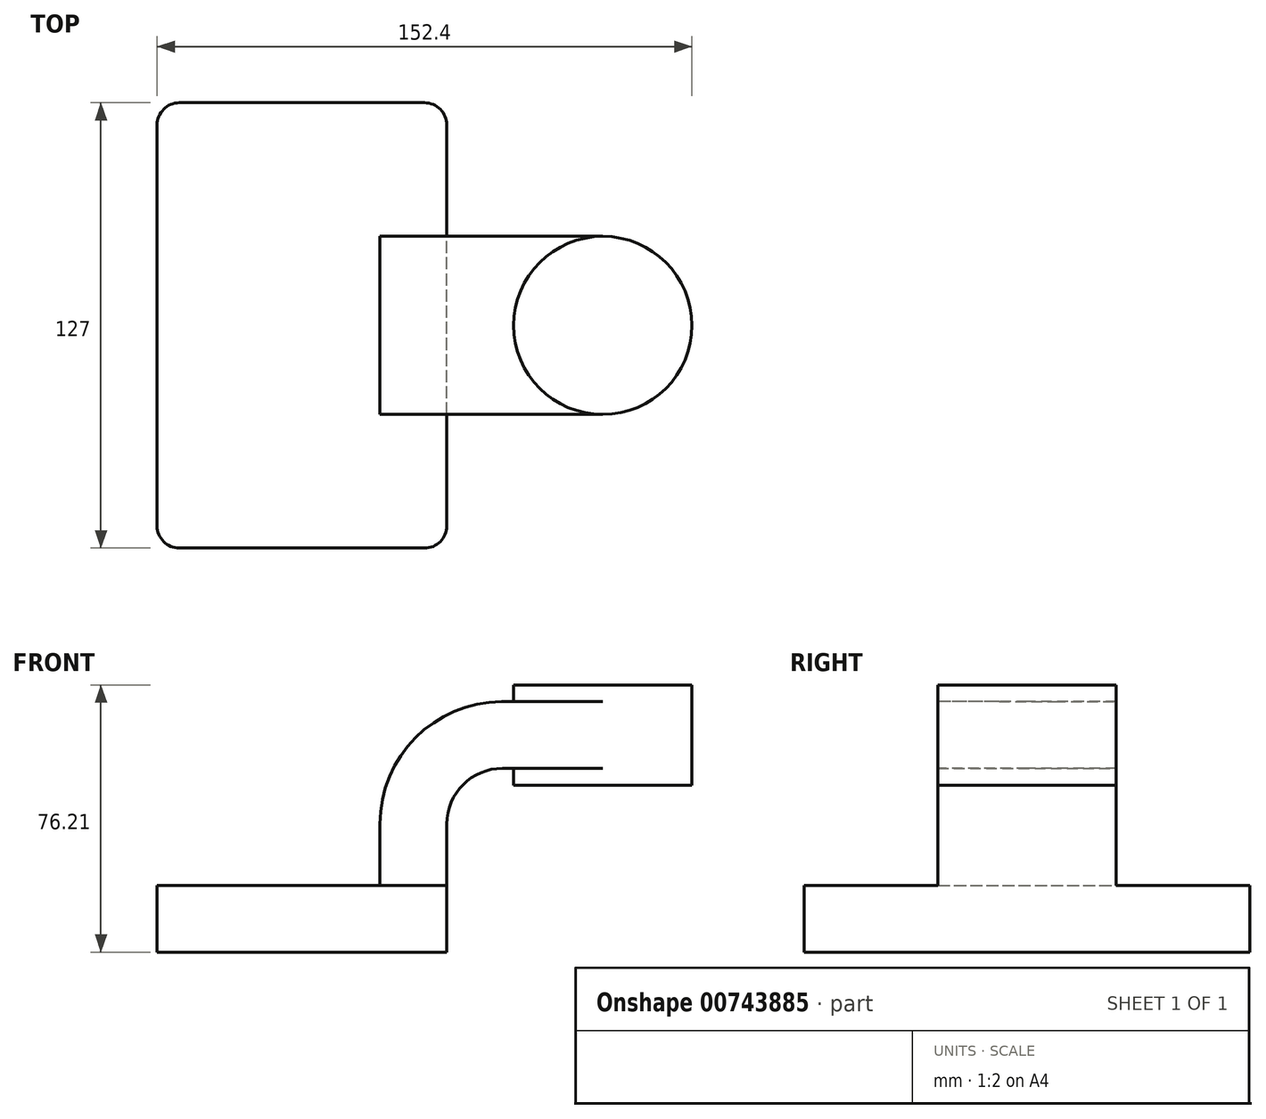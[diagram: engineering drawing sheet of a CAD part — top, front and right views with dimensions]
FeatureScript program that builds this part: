
annotation { "Feature Type Name" : "Feature", "Feature Type Description" : "" }
export const myFeature = defineFeature(function(context is Context, id is Id, definition is map)
    precondition{}
    {
        {
            var Q0;
            Q0=qCreatedBy(makeId("Front.planeOp"),FACE);
            var sketch = newSketch(context, id + "F0", { "sketchPlane" : qUnion([Q0])});
            skLineSegment(sketch, "E0.bottom", {"start": v(-41.28, -9.53) * mm, "end": v(41.28, -9.53) * mm});
            skLineSegment(sketch, "E0.top", {"start": v(-41.28, 9.53) * mm, "end": v(41.28, 9.53) * mm});
            skLineSegment(sketch, "E0.left", {"start": v(-41.28, -9.53) * mm, "end": v(-41.28, 9.53) * mm});
            skLineSegment(sketch, "E0.right", {"start": v(41.28, -9.53) * mm, "end": v(41.28, 9.53) * mm});
            skPoint(sketch, "E0.middle", {"position": v(0, 0) * mm});
            skLineSegment(sketch, "E1.bottom", {"start": v(60.33, 66.68) * mm, "end": v(111.12, 66.68) * mm});
            skLineSegment(sketch, "E1.top", {"start": v(60.33, 38.1) * mm, "end": v(111.12, 38.1) * mm});
            skLineSegment(sketch, "E1.left", {"start": v(60.33, 66.67) * mm, "end": v(60.33, 38.1) * mm});
            skLineSegment(sketch, "E1.right", {"start": v(111.12, 66.67) * mm, "end": v(111.12, 38.1) * mm});
            skPoint(sketch, "E1.middle", {"position": v(85.72, 52.39) * mm});
            skLineSegment(sketch, "E2", {"start": v(41.28, 9.53) * mm, "end": v(41.28, 27) * mm});
            skArc(sketch, "E3", {"start": v(41.28, 27) * mm, "mid": v(45.92, 38.23) * mm, "end": v(57.15, 42.88) * mm});
            skLineSegment(sketch, "E4", {"start": v(57.15, 42.88) * mm, "end": v(85.73, 42.88) * mm});
            skLineSegment(sketch, "E5.0", {"start": v(57.15, 61.93) * mm, "end": v(85.73, 61.93) * mm});
            skArc(sketch, "E5.1", {"start": v(22.23, 27) * mm, "mid": v(32.45, 51.7) * mm, "end": v(57.15, 61.93) * mm});
            skLineSegment(sketch, "E5.2", {"start": v(22.23, 9.53) * mm, "end": v(22.23, 27) * mm});
            skLineSegment(sketch, "E6", {"start": v(85.72, 38.1) * mm, "end": v(85.72, 66.68) * mm});
            skFitSpline(sketch, "E7", {"points": [v(-41.28, 9.53) * mm, v(57.15, 61.93) * mm], "startDerivative": vector(1.51, 60.09) * mm, "endDerivative": vector(129.28, 0.26) * mm});
            skSolve(sketch);
        }
        {
            var Q0;
            Q0=makeQuery(id+"F0.imprint","IMPRINT",FACE,{"disambiguationData":[TD([[makeQuery(id+"F0.imprint","IMPRINT",EDGE,{"derivedFrom":sQuery(id+"F0.wireOp",EDGE,"E0.bottom")}),1.0]])]});
            extrude(context, id + "F1", {"entities" : qUnion([Q0]), "endBound" : BoundingType.SYMMETRIC, "depth" : 127 * mm, "offsetDistance" : 25.4 * mm});
        }
        {
            var Q0;
            {var subQ5=sQuery(id+"F0.wireOp",EDGE,"E2");Q0=makeQuery(id+"F0.imprint","IMPRINT",FACE,{"disambiguationData":[TD([[makeQuery(id+"F0.imprint","IMPRINT",EDGE,{"derivedFrom":subQ5}),1.0]])]});}
            var Q1;
            {var subQ0=sQuery(id+"F0.wireOp",EDGE,"E5.0");var subQ1=sQuery(id+"F0.wireOp",EDGE,"E1.left");var subQ2=makeQuery(id+"F0.imprint","INTERSECT",VERTEX,{"derivedFrom":[subQ1,subQ0]});Q1=makeQuery(id+"F0.imprint","IMPRINT",FACE,{"disambiguationData":[TD([[makeQuery(id+"F0.imprint","IMPRINT",EDGE,{"disambiguationData":[TD([[subQ2,-1.0]])],"derivedFrom":subQ1}),1.0]])]});}
            extrude(context, id + "F2", {"entities" : qUnion([Q0, Q1]), "operationType" : NewBodyOperationType.ADD, "endBound" : BoundingType.SYMMETRIC, "depth" : 50.8 * mm, "offsetDistance" : 25.4 * mm});
        }
        {
            var Q0;
            {var subQ4=sQuery(id+"F0.wireOp",EDGE,"E5.1");Q0=makeQuery(id+"F0.imprint","IMPRINT",FACE,{"disambiguationData":[TD([[makeQuery(id+"F0.imprint","IMPRINT",EDGE,{"derivedFrom":subQ4}),1.0]])]});}
            extrude(context, id + "F3", {"entities" : qUnion([Q0]), "operationType" : NewBodyOperationType.ADD, "endBound" : BoundingType.SYMMETRIC, "depth" : 15.88 * mm, "offsetDistance" : 25.4 * mm});
        }
        {
            var Q0;
            {var subQ0=sQuery(id+"F0.wireOp",EDGE,"E1.right");Q0=makeQuery(id+"F0.imprint","IMPRINT",FACE,{"disambiguationData":[TD([[makeQuery(id+"F0.imprint","IMPRINT",EDGE,{"derivedFrom":subQ0}),-1.0]])]});}
            var Q1;
            Q1=sQuery(id+"F0.wireOp",EDGE,"E6");
            revolve(context, id + "F4", {"operationType" : NewBodyOperationType.ADD, "surfaceOperationType" : NewSurfaceOperationType.NEW, "entities" : qUnion([Q0]), "axis" : qUnion([Q1]), "revolveType" : RevolveType.FULL});
        }
        {
            var Q0;
            Q0=makeQuery(id+"F1.opExtrude","CAP_EDGE",EDGE,{"disambiguationData":[OSD([sQuery(id+"F0.wireOp",EDGE,"E0.right")])],"isStart":false});
            var Q1;
            Q1=makeQuery(id+"F1.opExtrude","CAP_EDGE",EDGE,{"disambiguationData":[OSD([sQuery(id+"F0.wireOp",EDGE,"E0.right")])],"isStart":true});
            var Q2;
            Q2=makeQuery(id+"F1.opExtrude","CAP_EDGE",EDGE,{"disambiguationData":[OSD([sQuery(id+"F0.wireOp",EDGE,"E0.left")])],"isStart":false});
            var Q3;
            Q3=makeQuery(id+"F1.opExtrude","CAP_EDGE",EDGE,{"disambiguationData":[OSD([sQuery(id+"F0.wireOp",EDGE,"E0.left")])],"isStart":true});
            fillet(context, id + "F5", {"entities" : qUnion([Q0, Q1, Q2, Q3]), "radius" : 6.35 * mm, "tangentPropagation" : true, "allowEdgeOverflow" : false});
        }
    });
